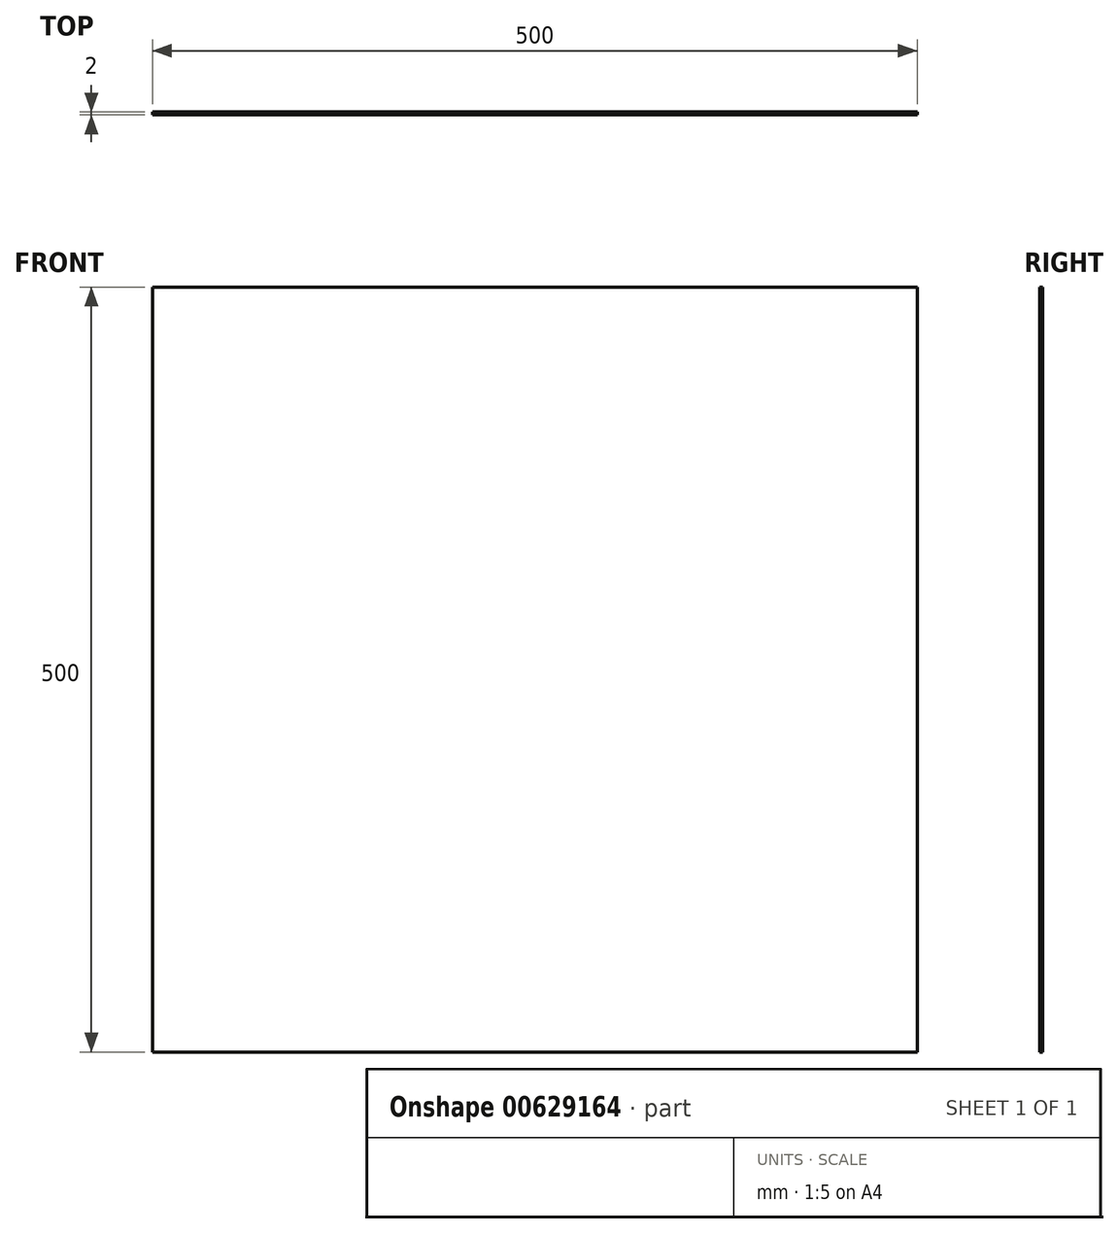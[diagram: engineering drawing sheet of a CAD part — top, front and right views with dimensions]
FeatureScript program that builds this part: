
annotation { "Feature Type Name" : "Feature", "Feature Type Description" : "" }
export const myFeature = defineFeature(function(context is Context, id is Id, definition is map)
    precondition{}
    {
        {
            var Q0;
            Q0=qCreatedBy(makeId("Front.planeOp"),FACE);
            var sketch = newSketch(context, id + "F0", { "sketchPlane" : qUnion([Q0])});
            skLineSegment(sketch, "E0.bottom", {"start": v(0, 0) * mm, "end": v(500, 0) * mm});
            skLineSegment(sketch, "E0.top", {"start": v(0, 500) * mm, "end": v(500, 500) * mm});
            skLineSegment(sketch, "E0.left", {"start": v(0, 0) * mm, "end": v(0, 500) * mm});
            skLineSegment(sketch, "E0.right", {"start": v(500, 0) * mm, "end": v(500, 500) * mm});
            skSolve(sketch);
        }
        {
            var Q0;
            Q0 = qSketchRegion(id + "F0", true);
            extrude(context, id + "F1", {"entities" : qUnion([Q0]), "depth" : 2 * mm, "offsetDistance" : 25 * mm});
        }
        {
            var Q0;
            Q0=makeQuery(id+"F1.opExtrude","SWEPT_FACE",FACE,{"disambiguationData":[OSD([sQuery(id+"F0.wireOp",EDGE,"E0.bottom")])]});
            var sketch = newSketch(context, id + "F2", { "sketchPlane" : qUnion([Q0])});
            skLineSegment(sketch, "E1", {"start": v(500, 1) * mm, "end": v(0, 1) * mm, "construction": true});
            skSolve(sketch);
        }
    });
